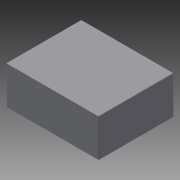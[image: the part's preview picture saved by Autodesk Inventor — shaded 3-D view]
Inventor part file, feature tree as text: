
AUTODESK INVENTOR PART (.ipt)
format: ipt  version: 2014 SP1 (Build 180222100, 222)  size: 89,088 bytes
history: native  units: in
note: dims shown in document units (in); Inventor stores cm internally (conversion verified against a paired STEP export)
features: reference x3, extrude x1, fillet x1, sketch x1
ambient origin geometry x8: Origin, YZ Plane, XZ Plane, XY Plane, X Axis, Y Axis, Z Axis, Center Point
bodies: Solid1 (feature_tree)
feature tree (6):
  extrude  "Extrusion1"  Depth=2.97in
  fillet  "Fillet1"  Radius=5.74in
  sketch  "Sketch1"  dims[d0=7.07in d1=2.97in d2=5.74in d3=0.0in d4=0.05in]
  reference  "Reference1"
  reference  "Reference2"
  reference  "Reference3"
